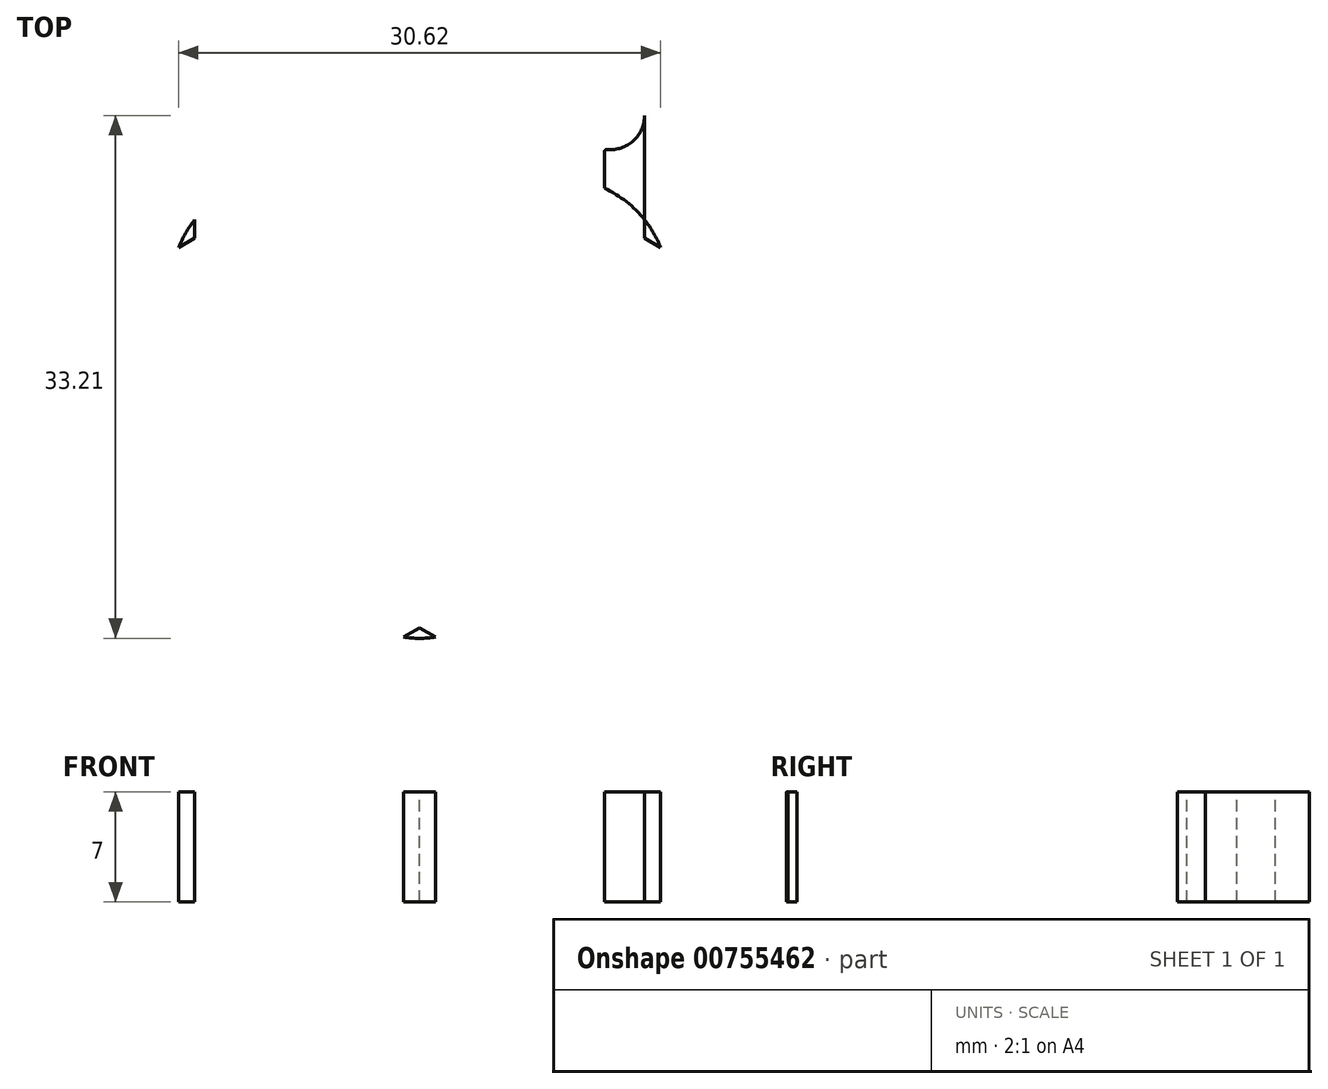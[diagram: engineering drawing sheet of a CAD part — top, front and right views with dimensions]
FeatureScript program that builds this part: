
annotation { "Feature Type Name" : "Feature", "Feature Type Description" : "" }
export const myFeature = defineFeature(function(context is Context, id is Id, definition is map)
    precondition{}
    {
        {
            var Q0;
            Q0=qCreatedBy(makeId("Top.planeOp"),FACE);
            var sketch = newSketch(context, id + "F0", { "sketchPlane" : qUnion([Q0])});
            skCircle(sketch, "E0.cCircle", {"center": v(0, 0) * mm, "radius": 8.25 * mm, "construction": true});
            skLineSegment(sketch, "E0.0", {"start": v(-14.29, 8.25) * mm, "end": v(14.29, 8.25) * mm});
            skLineSegment(sketch, "E0.1", {"start": v(14.29, 8.25) * mm, "end": v(0, -16.5) * mm});
            skLineSegment(sketch, "E0.2", {"start": v(0, -16.5) * mm, "end": v(-14.29, 8.25) * mm});
            skPoint(sketch, "E0.0.midPoint", {"position": v(0, 8.25) * mm});
            skSolve(sketch);
        }
        {
            var Q0;
            Q0 = qSketchRegion(id + "F0", true);
            extrude(context, id + "F1", {"entities" : qUnion([Q0]), "depth" : 7 * mm, "offsetDistance" : 25.4 * mm});
        }
        {
            var Q0;
            Q0=makeQuery(id+"F1.opExtrude","SWEPT_FACE",FACE,{"disambiguationData":[OSD([sQuery(id+"F0.wireOp",EDGE,"E0.2")])]});
            extrude(context, id + "F2", {"entities" : qUnion([Q0]), "operationType" : NewBodyOperationType.ADD, "depth" : 33.02 * mm, "offsetDistance" : 25.4 * mm});
        }
        {
            var Q0;
            Q0=makeQuery(id+"F1.opExtrude","SWEPT_FACE",FACE,{"disambiguationData":[OSD([sQuery(id+"F0.wireOp",EDGE,"E0.0")])]});
            extrude(context, id + "F3", {"entities" : qUnion([Q0]), "operationType" : NewBodyOperationType.ADD, "depth" : 33.02 * mm, "offsetDistance" : 25.4 * mm});
        }
        {
            var Q0;
            Q0=makeQuery(id+"F1.opExtrude","SWEPT_FACE",FACE,{"disambiguationData":[OSD([sQuery(id+"F0.wireOp",EDGE,"E0.1")])]});
            extrude(context, id + "F4", {"entities" : qUnion([Q0]), "operationType" : NewBodyOperationType.ADD, "depth" : 33.02 * mm, "offsetDistance" : 25.4 * mm});
        }
        {
            var Q0;
            {var subQ0=sQuery(id+"F0.wireOp",EDGE,"E0.1");var subQ1=sQuery(id+"F0.wireOp",EDGE,"E0.0");var subQ2=sQuery(id+"F0.wireOp",EDGE,"E0.2");Q0=makeQuery(id+"F4.boolean.opBoolean","MERGE",FACE,{"derivedFrom":[makeQuery(id+"F3.boolean.opBoolean","MERGE",FACE,{"derivedFrom":[makeQuery(id+"F2.boolean.opBoolean","MERGE",FACE,{"derivedFrom":[makeQuery(id+"F1.opExtrude","CAP_FACE",FACE,{"disambiguationData":[OSD([subQ1,subQ0,subQ2])],"isStart":false}),makeQuery(id+"F2.opExtrude","SWEPT_FACE",FACE,{"disambiguationData":[OSD([subQ2]),TDD([makeQuery(id+"F1.opExtrude","CAP_EDGE",EDGE,{"disambiguationData":[OSD([subQ2])],"isStart":false})])]})]}),makeQuery(id+"F3.opExtrude","SWEPT_FACE",FACE,{"disambiguationData":[OSD([subQ1]),TDD([makeQuery(id+"F1.opExtrude","CAP_EDGE",EDGE,{"disambiguationData":[OSD([subQ1])],"isStart":false})])]})]}),makeQuery(id+"F4.opExtrude","SWEPT_FACE",FACE,{"disambiguationData":[OSD([subQ0]),TDD([makeQuery(id+"F1.opExtrude","CAP_EDGE",EDGE,{"disambiguationData":[OSD([subQ0])],"isStart":false})])]})]});}
            var sketch = newSketch(context, id + "F5", { "sketchPlane" : qUnion([Q0])});
            skPoint(sketch, "E1", {"position": v(0, 41.27) * mm});
            skPoint(sketch, "E2", {"position": v(35.74, -20.63) * mm});
            skPoint(sketch, "E3", {"position": v(-35.74, -20.63) * mm});
            skLineSegment(sketch, "E4", {"start": v(35.74, -20.63) * mm, "end": v(23.64, -13.65) * mm});
            skLineSegment(sketch, "E5", {"start": v(-35.74, -20.63) * mm, "end": v(-23.64, -13.65) * mm});
            skCircle(sketch, "E6", {"center": v(0, 27.3) * mm, "radius": 11.25 * mm});
            skCircle(sketch, "E7", {"center": v(23.64, -13.65) * mm, "radius": 11.25 * mm});
            skCircle(sketch, "E8", {"center": v(-23.64, -13.65) * mm, "radius": 11.25 * mm});
            skCircle(sketch, "E9", {"center": v(0, 0) * mm, "radius": 11 * mm});
            skSolve(sketch);
        }
        {
            var Q0;
            Q0=makeQuery(id+"F2.opExtrude","CAP_EDGE",EDGE,{"disambiguationData":[OSD([sQuery(id+"F0.wireOp",EDGE,"E0.0"),sQuery(id+"F0.wireOp",EDGE,"E0.2")])],"isStart":false});
            var Q1;
            Q1=makeQuery(id+"F2.opExtrude","CAP_EDGE",EDGE,{"disambiguationData":[OSD([sQuery(id+"F0.wireOp",EDGE,"E0.1"),sQuery(id+"F0.wireOp",EDGE,"E0.2")])],"isStart":false});
            var Q2;
            Q2=makeQuery(id+"F4.opExtrude","CAP_EDGE",EDGE,{"disambiguationData":[OSD([sQuery(id+"F0.wireOp",EDGE,"E0.1"),sQuery(id+"F0.wireOp",EDGE,"E0.2")])],"isStart":false});
            var Q3;
            Q3=makeQuery(id+"F4.opExtrude","CAP_EDGE",EDGE,{"disambiguationData":[OSD([sQuery(id+"F0.wireOp",EDGE,"E0.0"),sQuery(id+"F0.wireOp",EDGE,"E0.1")])],"isStart":false});
            var Q4;
            Q4=makeQuery(id+"F3.opExtrude","CAP_EDGE",EDGE,{"disambiguationData":[OSD([sQuery(id+"F0.wireOp",EDGE,"E0.0"),sQuery(id+"F0.wireOp",EDGE,"E0.1")])],"isStart":false});
            var Q5;
            Q5=makeQuery(id+"F3.opExtrude","CAP_EDGE",EDGE,{"disambiguationData":[OSD([sQuery(id+"F0.wireOp",EDGE,"E0.0"),sQuery(id+"F0.wireOp",EDGE,"E0.2")])],"isStart":false});
            fillet(context, id + "F6", {"entities" : qUnion([Q0, Q1, Q2, Q3, Q4, Q5]), "radius" : 7.62 * mm, "tangentPropagation" : true, "defaultsChanged" : false, "vertexSettings" : [], "allowEdgeOverflow" : false});
        }
        {
            var Q0;
            Q0=makeQuery(id+"F5.imprint","IMPRINT",FACE,{"disambiguationData":[TD([[makeQuery(id+"F5.imprint","IMPRINT",EDGE,{"derivedFrom":sQuery(id+"F5.wireOp",EDGE,"E6")}),1.0]])]});
            var Q1;
            Q1=makeQuery(id+"F5.imprint","IMPRINT",FACE,{"disambiguationData":[TD([[makeQuery(id+"F5.imprint","IMPRINT",EDGE,{"derivedFrom":sQuery(id+"F5.wireOp",EDGE,"E9")}),1.0]])]});
            var Q2;
            Q2=makeQuery(id+"F5.imprint","IMPRINT",FACE,{"disambiguationData":[TD([[makeQuery(id+"F5.imprint","IMPRINT",EDGE,{"derivedFrom":sQuery(id+"F5.wireOp",EDGE,"E7")}),1.0]])]});
            var Q3;
            Q3=makeQuery(id+"F5.imprint","IMPRINT",FACE,{"disambiguationData":[TD([[makeQuery(id+"F5.imprint","IMPRINT",EDGE,{"derivedFrom":sQuery(id+"F5.wireOp",EDGE,"E8")}),1.0]])]});
            extrude(context, id + "F7", {"entities" : qUnion([Q0, Q1, Q2, Q3]), "operationType" : NewBodyOperationType.REMOVE, "oppositeDirection" : true, "depth" : 25.4 * mm, "offsetDistance" : 25.4 * mm});
        }
        {
            var Q0;
            {var subQ0=sQuery(id+"F0.wireOp",EDGE,"E0.1");var subQ1=sQuery(id+"F0.wireOp",EDGE,"E0.0");var subQ2=sQuery(id+"F0.wireOp",EDGE,"E0.2");Q0=makeQuery(id+"F4.boolean.opBoolean","MERGE",FACE,{"derivedFrom":[makeQuery(id+"F3.boolean.opBoolean","MERGE",FACE,{"derivedFrom":[makeQuery(id+"F2.boolean.opBoolean","MERGE",FACE,{"derivedFrom":[makeQuery(id+"F1.opExtrude","CAP_FACE",FACE,{"disambiguationData":[OSD([subQ1,subQ0,subQ2])],"isStart":false}),makeQuery(id+"F2.opExtrude","SWEPT_FACE",FACE,{"disambiguationData":[OSD([subQ2]),TDD([makeQuery(id+"F1.opExtrude","CAP_EDGE",EDGE,{"disambiguationData":[OSD([subQ2])],"isStart":false})])]})]}),makeQuery(id+"F3.opExtrude","SWEPT_FACE",FACE,{"disambiguationData":[OSD([subQ1]),TDD([makeQuery(id+"F1.opExtrude","CAP_EDGE",EDGE,{"disambiguationData":[OSD([subQ1])],"isStart":false})])]})]}),makeQuery(id+"F4.opExtrude","SWEPT_FACE",FACE,{"disambiguationData":[OSD([subQ0]),TDD([makeQuery(id+"F1.opExtrude","CAP_EDGE",EDGE,{"disambiguationData":[OSD([subQ0])],"isStart":false})])]})]});}
            var sketch = newSketch(context, id + "F8", { "sketchPlane" : qUnion([Q0])});
            skPoint(sketch, "E10.center", {"position": v(-6.67, -4.58) * mm});
            skLineSegment(sketch, "E11", {"start": v(14.04, -7.78) * mm, "end": v(21.35, 4.17) * mm});
            skPoint(sketch, "E12.center", {"position": v(0, 0) * mm});
            skLineSegment(sketch, "E13", {"start": v(0, 16.05) * mm, "end": v(-14.29, 16.05) * mm});
            skArc(sketch, "E14", {"start": v(-6.67, 41.27) * mm, "mid": v(-36.2, 30.5) * mm, "end": v(-51.85, 3.24) * mm});
            skArc(sketch, "E15", {"start": v(-14.29, 16.05) * mm, "mid": v(-36.05, 18.38) * mm, "end": v(-51.85, 3.24) * mm});
            skArc(sketch, "E16.1.0", {"start": v(-32.4, -26.4) * mm, "mid": v(-8.31, -46.6) * mm, "end": v(23.12, -46.52) * mm});
            skArc(sketch, "E16.1.1", {"start": v(-6.75, -20.4) * mm, "mid": v(2.1, -40.4) * mm, "end": v(23.12, -46.52) * mm});
            skArc(sketch, "E16.2.0", {"start": v(39.07, -14.86) * mm, "mid": v(44.5, 16.1) * mm, "end": v(28.73, 43.28) * mm});
            skArc(sketch, "E16.2.1", {"start": v(21.04, 4.35) * mm, "mid": v(33.94, 22.03) * mm, "end": v(28.73, 43.28) * mm});
            skCircle(sketch, "E17", {"center": v(-21.52, 28.91) * mm, "radius": 4.4 * mm});
            skCircle(sketch, "E18", {"center": v(-32.52, 26.04) * mm, "radius": 2.64 * mm});
            skCircle(sketch, "E19", {"center": v(-40.16, 21.05) * mm, "radius": 1.87 * mm});
            skCircle(sketch, "E20.1.0", {"center": v(-14.28, -33.1) * mm, "radius": 4.4 * mm});
            skCircle(sketch, "E20.1.1", {"center": v(-6.29, -41.18) * mm, "radius": 2.64 * mm});
            skCircle(sketch, "E20.1.2", {"center": v(1.85, -45.3) * mm, "radius": 1.87 * mm});
            skCircle(sketch, "E20.2.0", {"center": v(35.8, 4.18) * mm, "radius": 4.4 * mm});
            skCircle(sketch, "E20.2.1", {"center": v(38.8, 15.15) * mm, "radius": 2.64 * mm});
            skCircle(sketch, "E20.2.2", {"center": v(38.3, 24.26) * mm, "radius": 1.87 * mm});
            skSolve(sketch);
        }
        {
            var Q0;
            Q0=makeQuery(id+"F8.imprint","IMPRINT",FACE,{"disambiguationData":[TD([[makeQuery(id+"F8.imprint","IMPRINT",EDGE,{"derivedFrom":sQuery(id+"F8.wireOp",EDGE,"E14")}),1.0]])]});
            var Q1;
            Q1=makeQuery(id+"F8.imprint","IMPRINT",FACE,{"disambiguationData":[TD([[makeQuery(id+"F8.imprint","IMPRINT",EDGE,{"derivedFrom":sQuery(id+"F8.wireOp",EDGE,"E16.1.0")}),1.0]])]});
            var Q2;
            Q2=makeQuery(id+"F8.imprint","IMPRINT",FACE,{"disambiguationData":[TD([[makeQuery(id+"F8.imprint","IMPRINT",EDGE,{"derivedFrom":sQuery(id+"F8.wireOp",EDGE,"E16.2.0")}),1.0]])]});
            extrude(context, id + "F9", {"entities" : qUnion([Q0, Q1, Q2]), "operationType" : NewBodyOperationType.ADD, "oppositeDirection" : true, "depth" : 7 * mm, "offsetDistance" : 25.4 * mm});
        }
        {
            var Q0;
            Q0=makeQuery(id+"F9.opExtrude","SWEPT_EDGE",EDGE,{"disambiguationData":[OSD([sQuery(id+"F8.wireOp",EDGE,"E16.2.0"),sQuery(id+"F8.wireOp",EDGE,"E16.2.1")])]});
            var Q1;
            Q1=makeQuery(id+"F9.opExtrude","SWEPT_EDGE",EDGE,{"disambiguationData":[OSD([sQuery(id+"F8.wireOp",EDGE,"E16.1.0"),sQuery(id+"F8.wireOp",EDGE,"E16.1.1")])]});
            var Q2;
            Q2=makeQuery(id+"F9.opExtrude","SWEPT_EDGE",EDGE,{"disambiguationData":[OSD([sQuery(id+"F8.wireOp",EDGE,"E14"),sQuery(id+"F8.wireOp",EDGE,"E15")])]});
            fillet(context, id + "F10", {"entities" : qUnion([Q0, Q1, Q2]), "radius" : 1.27 * mm, "tangentPropagation" : true, "defaultsChanged" : false, "vertexSettings" : [], "allowEdgeOverflow" : false});
        }
        {
            var Q0;
            {var subQ0=sQuery(id+"F0.wireOp",EDGE,"E0.2");var subQ1=sQuery(id+"F0.wireOp",EDGE,"E0.1");var subQ2=sQuery(id+"F0.wireOp",EDGE,"E0.0");Q0=makeQuery(id+"F9.boolean.opBoolean","MERGE",FACE,{"derivedFrom":[makeQuery(id+"F4.boolean.opBoolean","MERGE",FACE,{"derivedFrom":[makeQuery(id+"F3.boolean.opBoolean","MERGE",FACE,{"derivedFrom":[makeQuery(id+"F2.boolean.opBoolean","MERGE",FACE,{"derivedFrom":[makeQuery(id+"F1.opExtrude","CAP_FACE",FACE,{"disambiguationData":[OSD([subQ2,subQ1,subQ0])],"isStart":false}),makeQuery(id+"F2.opExtrude","SWEPT_FACE",FACE,{"disambiguationData":[OSD([subQ0]),TDD([makeQuery(id+"F1.opExtrude","CAP_EDGE",EDGE,{"disambiguationData":[OSD([subQ0])],"isStart":false})])]})]}),makeQuery(id+"F3.opExtrude","SWEPT_FACE",FACE,{"disambiguationData":[OSD([subQ2]),TDD([makeQuery(id+"F1.opExtrude","CAP_EDGE",EDGE,{"disambiguationData":[OSD([subQ2])],"isStart":false})])]})]}),makeQuery(id+"F4.opExtrude","SWEPT_FACE",FACE,{"disambiguationData":[OSD([subQ1]),TDD([makeQuery(id+"F1.opExtrude","CAP_EDGE",EDGE,{"disambiguationData":[OSD([subQ1])],"isStart":false})])]})]}),makeQuery(id+"F9.opExtrude","CAP_FACE",FACE,{"disambiguationData":[OSD([subQ2,subQ1,subQ0,sQuery(id+"F8.wireOp",EDGE,"E14"),sQuery(id+"F8.wireOp",EDGE,"E15"),sQuery(id+"F8.wireOp",EDGE,"E17"),sQuery(id+"F8.wireOp",EDGE,"E18"),sQuery(id+"F8.wireOp",EDGE,"E19")])],"isStart":true}),makeQuery(id+"F9.opExtrude","CAP_FACE",FACE,{"disambiguationData":[OSD([subQ2,subQ1,subQ0,sQuery(id+"F8.wireOp",EDGE,"E16.1.0"),sQuery(id+"F8.wireOp",EDGE,"E16.1.1"),sQuery(id+"F8.wireOp",EDGE,"E20.1.0"),sQuery(id+"F8.wireOp",EDGE,"E20.1.1"),sQuery(id+"F8.wireOp",EDGE,"E20.1.2")])],"isStart":true}),makeQuery(id+"F9.opExtrude","CAP_FACE",FACE,{"disambiguationData":[OSD([subQ2,subQ1,subQ0,sQuery(id+"F8.wireOp",EDGE,"E16.2.0"),sQuery(id+"F8.wireOp",EDGE,"E16.2.1"),sQuery(id+"F8.wireOp",EDGE,"E20.2.0"),sQuery(id+"F8.wireOp",EDGE,"E20.2.1"),sQuery(id+"F8.wireOp",EDGE,"E20.2.2")])],"isStart":true})]});}
            var sketch = newSketch(context, id + "F11", { "sketchPlane" : qUnion([Q0])});
            skArc(sketch, "E21", {"start": v(-14.29, 16.05) * mm, "mid": v(-13.58, 14.44) * mm, "end": v(-11.9, 13.9) * mm});
            skArc(sketch, "E22", {"start": v(-11.73, 13.73) * mm, "mid": v(-11.78, 13.85) * mm, "end": v(-11.9, 13.9) * mm});
            skLineSegment(sketch, "E23", {"start": v(-11.73, 13.73) * mm, "end": v(-11.73, 11.42) * mm});
            skArc(sketch, "E24.MirrorCS", {"start": v(11.73, 13.73) * mm, "mid": v(11.78, 13.85) * mm, "end": v(11.9, 13.9) * mm});
            skArc(sketch, "E25.MirrorCS", {"start": v(14.29, 16.05) * mm, "mid": v(13.58, 14.44) * mm, "end": v(11.9, 13.9) * mm});
            skLineSegment(sketch, "E26.MirrorCS", {"start": v(11.73, 13.73) * mm, "end": v(11.73, 11.42) * mm});
            skLineSegment(sketch, "E27.1.0", {"start": v(-17.76, 3.3) * mm, "end": v(-15.76, 4.45) * mm});
            skLineSegment(sketch, "E27.1.1", {"start": v(-6.03, -17.03) * mm, "end": v(-4.03, -15.87) * mm});
            skArc(sketch, "E27.1.2", {"start": v(-6.75, -20.4) * mm, "mid": v(-5.72, -18.98) * mm, "end": v(-6.08, -17.26) * mm});
            skArc(sketch, "E27.1.3", {"start": v(-21.04, 4.35) * mm, "mid": v(-19.3, 4.54) * mm, "end": v(-17.98, 3.37) * mm});
            skArc(sketch, "E27.1.4", {"start": v(-17.76, 3.3) * mm, "mid": v(-17.89, 3.28) * mm, "end": v(-17.98, 3.37) * mm});
            skArc(sketch, "E27.1.5", {"start": v(-6.03, -17.03) * mm, "mid": v(-6.1, -17.13) * mm, "end": v(-6.08, -17.26) * mm});
            skLineSegment(sketch, "E27.2.0", {"start": v(6.03, -17.03) * mm, "end": v(4.03, -15.87) * mm});
            skLineSegment(sketch, "E27.2.1", {"start": v(17.76, 3.3) * mm, "end": v(15.76, 4.45) * mm});
            skArc(sketch, "E27.2.2", {"start": v(21.04, 4.35) * mm, "mid": v(19.3, 4.54) * mm, "end": v(17.98, 3.37) * mm});
            skArc(sketch, "E27.2.3", {"start": v(6.75, -20.4) * mm, "mid": v(5.72, -18.98) * mm, "end": v(6.08, -17.26) * mm});
            skArc(sketch, "E27.2.4", {"start": v(6.03, -17.03) * mm, "mid": v(6.1, -17.13) * mm, "end": v(6.08, -17.26) * mm});
            skArc(sketch, "E27.2.5", {"start": v(17.76, 3.3) * mm, "mid": v(17.89, 3.28) * mm, "end": v(17.98, 3.37) * mm});
            skPoint(sketch, "E27.center", {"position": v(0, 0) * mm});
            skArc(sketch, "E28", {"start": v(-11.73, 11.42) * mm, "mid": v(-14.86, 8.58) * mm, "end": v(-15.76, 4.45) * mm});
            skArc(sketch, "E29.1.0", {"start": v(-4.03, -15.87) * mm, "mid": v(0, -17.16) * mm, "end": v(4.03, -15.87) * mm});
            skArc(sketch, "E29.2.0", {"start": v(15.76, 4.45) * mm, "mid": v(14.86, 8.58) * mm, "end": v(11.73, 11.42) * mm});
            skSolve(sketch);
        }
        {
            var Q0;
            {var subQ1=sQuery(id+"F11.wireOp",EDGE,"E27.1.0");Q0=makeQuery(id+"F11.imprint","IMPRINT",FACE,{"disambiguationData":[TD([[makeQuery(id+"F11.imprint","IMPRINT",EDGE,{"derivedFrom":subQ1}),1.0]])]});}
            var Q1;
            {var subQ7=sQuery(id+"F11.wireOp",EDGE,"E21");Q1=makeQuery(id+"F11.imprint","IMPRINT",FACE,{"disambiguationData":[TD([[makeQuery(id+"F11.imprint","IMPRINT",EDGE,{"derivedFrom":subQ7}),-1.0]])]});}
            var Q2;
            {var subQ1=sQuery(id+"F11.wireOp",EDGE,"E27.1.1");Q2=makeQuery(id+"F11.imprint","IMPRINT",FACE,{"disambiguationData":[TD([[makeQuery(id+"F11.imprint","IMPRINT",EDGE,{"derivedFrom":subQ1}),-1.0]])]});}
            var Q3;
            {var subQ1=sQuery(id+"F11.wireOp",EDGE,"E27.2.0");Q3=makeQuery(id+"F11.imprint","IMPRINT",FACE,{"disambiguationData":[TD([[makeQuery(id+"F11.imprint","IMPRINT",EDGE,{"derivedFrom":subQ1}),1.0]])]});}
            var Q4;
            {var subQ1=sQuery(id+"F11.wireOp",EDGE,"E27.2.1");Q4=makeQuery(id+"F11.imprint","IMPRINT",FACE,{"disambiguationData":[TD([[makeQuery(id+"F11.imprint","IMPRINT",EDGE,{"derivedFrom":subQ1}),-1.0]])]});}
            var Q5;
            Q5=makeQuery(id+"F11.imprint","IMPRINT",FACE,{"disambiguationData":[TD([[makeQuery(id+"F11.imprint","IMPRINT",EDGE,{"derivedFrom":sQuery(id+"F11.wireOp",EDGE,"E24.MirrorCS")}),-1.0]])]});
            extrude(context, id + "F12", {"entities" : qUnion([Q0, Q1, Q2, Q3, Q4, Q5]), "operationType" : NewBodyOperationType.REMOVE, "oppositeDirection" : true, "depth" : 25.4 * mm, "offsetDistance" : 25.4 * mm});
        }
        {
            var Q0;
            {var subQ0=sQuery(id+"F11.wireOp",EDGE,"E28");var subQ1=sQuery(id+"F0.wireOp",EDGE,"E0.2");var subQ2=sQuery(id+"F0.wireOp",EDGE,"E0.0");var subQ3=makeQuery(id+"F1.opExtrude","CAP_VERTEX",VERTEX,{"disambiguationData":[OSD([subQ2,subQ1])],"isStart":false});var subQ6=makeQuery(id+"F2.opExtrude","SWEPT_EDGE",EDGE,{"disambiguationData":[OSD([subQ2,subQ1]),TDD([subQ3])]});var subQ7=makeQuery(id+"F11.imprint","INTERSECT",VERTEX,{"derivedFrom":[subQ6,subQ0]});Q0=makeQuery(id+"F11.imprint","IMPRINT",FACE,{"disambiguationData":[TD([[makeQuery(id+"F11.imprint","IMPRINT",EDGE,{"disambiguationData":[TD([[subQ7,1.0]])],"derivedFrom":subQ0}),1.0]])]});}
            var Q1;
            {var subQ0=sQuery(id+"F11.wireOp",EDGE,"E29.1.0");var subQ1=sQuery(id+"F0.wireOp",EDGE,"E0.2");var subQ2=sQuery(id+"F0.wireOp",EDGE,"E0.1");var subQ3=makeQuery(id+"F1.opExtrude","CAP_VERTEX",VERTEX,{"disambiguationData":[OSD([subQ2,subQ1])],"isStart":false});var subQ4=makeQuery(id+"F2.opExtrude","SWEPT_EDGE",EDGE,{"disambiguationData":[OSD([subQ2,subQ1]),TDD([subQ3])]});var subQ5=makeQuery(id+"F11.imprint","INTERSECT",VERTEX,{"derivedFrom":[subQ4,subQ0]});Q1=makeQuery(id+"F11.imprint","IMPRINT",FACE,{"disambiguationData":[TD([[makeQuery(id+"F11.imprint","IMPRINT",EDGE,{"disambiguationData":[TD([[subQ5,-1.0]])],"derivedFrom":subQ0}),1.0]])]});}
            var Q2;
            {var subQ0=sQuery(id+"F11.wireOp",EDGE,"E29.2.0");var subQ1=sQuery(id+"F0.wireOp",EDGE,"E0.1");var subQ2=sQuery(id+"F0.wireOp",EDGE,"E0.0");var subQ3=makeQuery(id+"F1.opExtrude","CAP_VERTEX",VERTEX,{"disambiguationData":[OSD([subQ2,subQ1])],"isStart":false});var subQ6=makeQuery(id+"F3.opExtrude","SWEPT_EDGE",EDGE,{"disambiguationData":[OSD([subQ2,subQ1]),TDD([subQ3])]});var subQ7=makeQuery(id+"F11.imprint","INTERSECT",VERTEX,{"derivedFrom":[subQ6,subQ0]});Q2=makeQuery(id+"F11.imprint","IMPRINT",FACE,{"disambiguationData":[TD([[makeQuery(id+"F11.imprint","IMPRINT",EDGE,{"disambiguationData":[TD([[subQ7,1.0]])],"derivedFrom":subQ0}),1.0]])]});}
            extrude(context, id + "F13", {"entities" : qUnion([Q0, Q1, Q2]), "operationType" : NewBodyOperationType.ADD, "depth" : -7 * mm, "offsetDistance" : 25.4 * mm});
        }
    });
